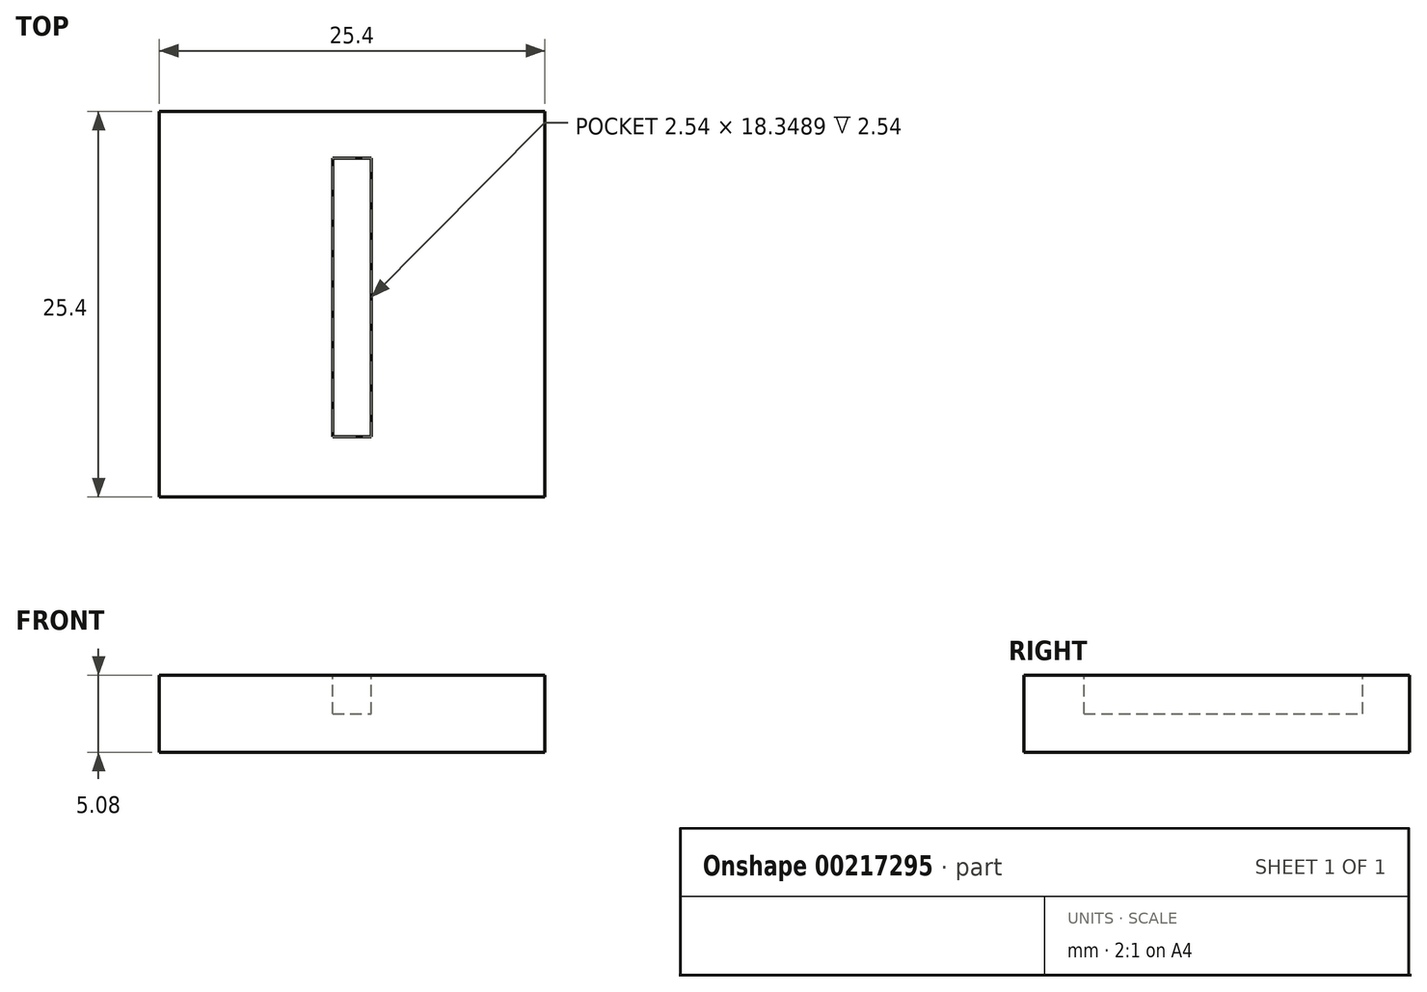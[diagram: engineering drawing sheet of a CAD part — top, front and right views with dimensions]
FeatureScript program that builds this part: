
annotation { "Feature Type Name" : "Feature", "Feature Type Description" : "" }
export const myFeature = defineFeature(function(context is Context, id is Id, definition is map)
    precondition{}
    {
        {
            var Q0;
            Q0=qCreatedBy(makeId("Top.planeOp"),FACE);
            var sketch = newSketch(context, id + "F0", { "sketchPlane" : qUnion([Q0])});
            skLineSegment(sketch, "E0.bottom", {"start": v(12.7, -12.7) * mm, "end": v(-12.7, -12.7) * mm});
            skLineSegment(sketch, "E0.top", {"start": v(12.7, 12.7) * mm, "end": v(-12.7, 12.7) * mm});
            skLineSegment(sketch, "E0.left", {"start": v(12.7, -12.7) * mm, "end": v(12.7, 12.7) * mm});
            skLineSegment(sketch, "E0.right", {"start": v(-12.7, -12.7) * mm, "end": v(-12.7, 12.7) * mm});
            skPoint(sketch, "E0.middle", {"position": v(0, 0) * mm});
            skSolve(sketch);
        }
        {
            var Q0;
            Q0=qSketchRegion(id+"F0",true);
            extrude(context, id + "F1", {"entities" : qUnion([Q0]), "depth" : 5.08 * mm});
        }
        {
            var Q0;
            Q0=makeQuery(id+"F1.opExtrude","CAP_FACE",FACE,{"disambiguationData":[OSD([sQuery(id+"F0.wireOp",EDGE,"E0.bottom"),sQuery(id+"F0.wireOp",EDGE,"E0.top"),sQuery(id+"F0.wireOp",EDGE,"E0.left"),sQuery(id+"F0.wireOp",EDGE,"E0.right")])],"isStart":false});
            var sketch = newSketch(context, id + "F2", { "sketchPlane" : qUnion([Q0])});
            skLineSegment(sketch, "E1.left", {"start": v(1.27, -8.73) * mm, "end": v(1.27, 9.62) * mm});
            skLineSegment(sketch, "E1.right", {"start": v(-1.27, -8.73) * mm, "end": v(-1.27, 9.62) * mm});
            skPoint(sketch, "E1.middle", {"position": v(0, 0) * mm});
            skLineSegment(sketch, "E2", {"start": v(-1.27, 9.62) * mm, "end": v(1.27, 9.62) * mm});
            skLineSegment(sketch, "E3", {"start": v(-1.27, -8.73) * mm, "end": v(1.27, -8.73) * mm});
            skPoint(sketch, "E1.top.end.orphan", {"position": v(-1.27, 12.7) * mm});
            skPoint(sketch, "E1.top.start.orphan", {"position": v(1.27, 12.7) * mm});
            skPoint(sketch, "E4.orphan", {"position": v(-1.27, -12.7) * mm});
            skPoint(sketch, "E5.orphan", {"position": v(1.27, -12.7) * mm});
            skSolve(sketch);
        }
        {
            var Q0;
            Q0=qSketchRegion(id+"F2",true);
            extrude(context, id + "F3", {"entities" : qUnion([Q0]), "operationType" : NewBodyOperationType.REMOVE, "oppositeDirection" : true, "depth" : 2.54 * mm});
        }
    });
